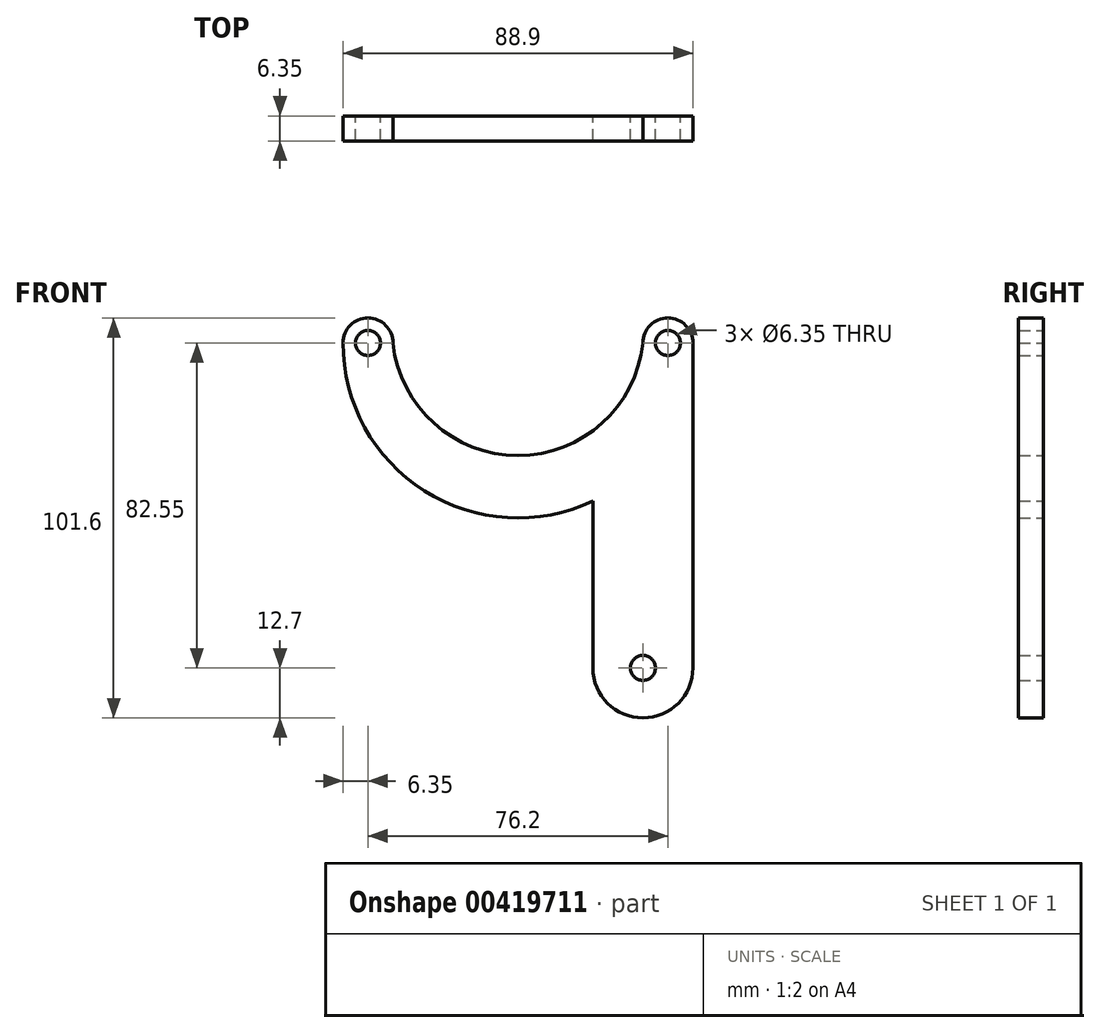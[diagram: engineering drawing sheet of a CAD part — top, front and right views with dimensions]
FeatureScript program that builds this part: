
annotation { "Feature Type Name" : "Feature", "Feature Type Description" : "" }
export const myFeature = defineFeature(function(context is Context, id is Id, definition is map)
    precondition{}
    {
        {
            var Q0;
            Q0=qCreatedBy(makeId("Front.planeOp"),FACE);
            var sketch = newSketch(context, id + "F0", { "sketchPlane" : qUnion([Q0])});
            skLineSegment(sketch, "E0", {"start": v(0, 0) * mm, "end": v(38.1, 0) * mm});
            skLineSegment(sketch, "E1", {"start": v(38.1, 0) * mm, "end": v(0, 0) * mm});
            skLineSegment(sketch, "E2", {"start": v(-38.1, 0) * mm, "end": v(0, 0) * mm});
            skCircle(sketch, "E3", {"center": v(-38.1, 0) * mm, "radius": 6.35 * mm});
            skCircle(sketch, "E4", {"center": v(38.1, 0) * mm, "radius": 6.35 * mm});
            skCircle(sketch, "E5", {"center": v(0, 0) * mm, "radius": 44.45 * mm});
            skLineSegment(sketch, "E6", {"start": v(0, 0) * mm, "end": v(0, -28.58) * mm});
            skLineSegment(sketch, "E7", {"start": v(-38.1, 0) * mm, "end": v(-31.75, 0) * mm});
            skLineSegment(sketch, "E8", {"start": v(38.1, 0) * mm, "end": v(31.75, 0) * mm});
            skArc(sketch, "E9", {"start": v(-31.75, 0) * mm, "mid": v(0, -28.58) * mm, "end": v(31.75, 0) * mm});
            skLineSegment(sketch, "E10", {"start": v(31.75, 0) * mm, "end": v(31.75, -82.55) * mm});
            skPoint(sketch, "E11", {"position": v(31.75, -82.55) * mm});
            skLineSegment(sketch, "E12", {"start": v(0, -44.45) * mm, "end": v(44.45, -44.45) * mm});
            skLineSegment(sketch, "E13", {"start": v(0, -44.45) * mm, "end": v(-52.8, -44.45) * mm});
            skCircle(sketch, "E14", {"center": v(31.75, -82.55) * mm, "radius": 12.7 * mm});
            skLineSegment(sketch, "E15", {"start": v(31.75, -82.55) * mm, "end": v(19.05, -82.55) * mm});
            skLineSegment(sketch, "E16", {"start": v(31.75, -82.55) * mm, "end": v(44.45, -82.55) * mm});
            skLineSegment(sketch, "E17", {"start": v(44.45, -82.55) * mm, "end": v(44.45, 0) * mm});
            skLineSegment(sketch, "E18", {"start": v(19.05, -82.55) * mm, "end": v(19.05, -40.16) * mm});
            skSolve(sketch);
        }
        {
            var Q0;
            {var subQ0=sQuery(id+"F0.wireOp",EDGE,"E3");var subQ2=makeQuery(id+"F0.imprint","INTERSECT",VERTEX,{"derivedFrom":[subQ0,sQuery(id+"F0.wireOp",EDGE,"E5")]});Q0=makeQuery(id+"F0.imprint","IMPRINT",FACE,{"disambiguationData":[TD([[makeQuery(id+"F0.imprint","IMPRINT",EDGE,{"disambiguationData":[TD([[subQ2,1.0]])],"derivedFrom":subQ0}),1.0]])]});}
            var Q1;
            {var subQ4=sQuery(id+"F0.wireOp",EDGE,"E5");var subQ5=makeQuery(id+"F0.imprint","INTERSECT",VERTEX,{"derivedFrom":[subQ4,sQuery(id+"F0.wireOp",EDGE,"XhDido47-JSk9-PN7a-mwUm-eUsiFU9qKRD5")]});Q1=makeQuery(id+"F0.imprint","IMPRINT",FACE,{"disambiguationData":[TD([[makeQuery(id+"F0.imprint","IMPRINT",EDGE,{"disambiguationData":[TD([[subQ5,1.0]])],"derivedFrom":subQ4}),1.0]])]});}
            var Q2;
            {var subQ0=sQuery(id+"F0.wireOp",EDGE,"E4");var subQ2=makeQuery(id+"F0.imprint","INTERSECT",VERTEX,{"derivedFrom":[subQ0,sQuery(id+"F0.wireOp",EDGE,"E5"),sQuery(id+"F0.wireOp",EDGE,"RHOj4S1e-cnUz-p6yP-vj5Y-QZDLPZyhU6kP")]});Q2=makeQuery(id+"F0.imprint","IMPRINT",FACE,{"disambiguationData":[TD([[makeQuery(id+"F0.imprint","IMPRINT",EDGE,{"disambiguationData":[TD([[subQ2,-1.0]])],"derivedFrom":subQ0}),1.0]])]});}
            var Q3;
            {var subQ0=sQuery(id+"F0.wireOp",EDGE,"E10");var subQ3=sQuery(id+"F0.wireOp",EDGE,"E5");var subQ5=makeQuery(id+"F0.imprint","INTERSECT",VERTEX,{"derivedFrom":[subQ3,subQ0]});Q3=makeQuery(id+"F0.imprint","IMPRINT",FACE,{"disambiguationData":[TD([[makeQuery(id+"F0.imprint","IMPRINT",EDGE,{"disambiguationData":[TD([[subQ5,-1.0]])],"derivedFrom":subQ3}),1.0]])]});}
            var Q4;
            {var subQ0=sQuery(id+"F0.wireOp",EDGE,"RHOj4S1e-cnUz-p6yP-vj5Y-QZDLPZyhU6kP");Q4=makeQuery(id+"F0.imprint","IMPRINT",FACE,{"disambiguationData":[TD([[makeQuery(id+"F0.imprint","IMPRINT",EDGE,{"derivedFrom":subQ0}),-1.0]])]});}
            var Q5;
            {var subQ0=sQuery(id+"F0.wireOp",EDGE,"XhDido47-JSk9-PN7a-mwUm-eUsiFU9qKRD5");Q5=makeQuery(id+"F0.imprint","IMPRINT",FACE,{"disambiguationData":[TD([[makeQuery(id+"F0.imprint","IMPRINT",EDGE,{"derivedFrom":subQ0}),-1.0]])]});}
            var Q6;
            {var subQ0=sQuery(id+"F0.wireOp",EDGE,"3i2DmJEj-DKhP-iJt3-PwoP-cG0X3qstrTAl");Q6=makeQuery(id+"F0.imprint","IMPRINT",FACE,{"disambiguationData":[TD([[makeQuery(id+"F0.imprint","IMPRINT",EDGE,{"derivedFrom":subQ0}),-1.0]])]});}
            var Q7;
            {var subQ0=sQuery(id+"F0.wireOp",EDGE,"CGOJktKc-CADg-FGEi-2G2Y-Sdd0SxkiLkLI");Q7=makeQuery(id+"F0.imprint","IMPRINT",FACE,{"disambiguationData":[TD([[makeQuery(id+"F0.imprint","IMPRINT",EDGE,{"derivedFrom":subQ0}),1.0]])]});}
            var Q8;
            {var subQ0=sQuery(id+"F0.wireOp",EDGE,"3i2DmJEj-DKhP-iJt3-PwoP-cG0X3qstrTAl");Q8=makeQuery(id+"F0.imprint","IMPRINT",FACE,{"disambiguationData":[TD([[makeQuery(id+"F0.imprint","IMPRINT",EDGE,{"derivedFrom":subQ0}),1.0]])]});}
            var Q9;
            {var subQ0=sQuery(id+"F0.wireOp",EDGE,"E18");var subQ1=sQuery(id+"F0.wireOp",EDGE,"E5");var subQ2=makeQuery(id+"F0.imprint","INTERSECT",VERTEX,{"derivedFrom":[subQ1,subQ0]});Q9=makeQuery(id+"F0.imprint","IMPRINT",FACE,{"disambiguationData":[TD([[makeQuery(id+"F0.imprint","IMPRINT",EDGE,{"disambiguationData":[TD([[subQ2,-1.0]])],"derivedFrom":subQ1}),-1.0]])]});}
            var Q10;
            {var subQ1=sQuery(id+"F0.wireOp",EDGE,"E5");var subQ3=sQuery(id+"F0.wireOp",EDGE,"E10");var subQ4=makeQuery(id+"F0.imprint","INTERSECT",VERTEX,{"derivedFrom":[subQ1,subQ3]});Q10=makeQuery(id+"F0.imprint","IMPRINT",FACE,{"disambiguationData":[TD([[makeQuery(id+"F0.imprint","IMPRINT",EDGE,{"disambiguationData":[TD([[subQ4,-1.0]])],"derivedFrom":subQ3}),1.0]])]});}
            var Q11;
            {var subQ0=sQuery(id+"F0.wireOp",EDGE,"E12");var subQ1=sQuery(id+"F0.wireOp",EDGE,"E10");var subQ2=makeQuery(id+"F0.imprint","INTERSECT",VERTEX,{"derivedFrom":[subQ1,subQ0]});Q11=makeQuery(id+"F0.imprint","IMPRINT",FACE,{"disambiguationData":[TD([[makeQuery(id+"F0.imprint","IMPRINT",EDGE,{"disambiguationData":[TD([[subQ2,-1.0]])],"derivedFrom":subQ1}),1.0]])]});}
            var Q12;
            {var subQ0=sQuery(id+"F0.wireOp",EDGE,"E12");var subQ1=sQuery(id+"F0.wireOp",EDGE,"E10");var subQ2=makeQuery(id+"F0.imprint","INTERSECT",VERTEX,{"derivedFrom":[subQ1,subQ0]});Q12=makeQuery(id+"F0.imprint","IMPRINT",FACE,{"disambiguationData":[TD([[makeQuery(id+"F0.imprint","IMPRINT",EDGE,{"disambiguationData":[TD([[subQ2,-1.0]])],"derivedFrom":subQ1}),-1.0]])]});}
            var Q13;
            {var subQ0=sQuery(id+"F0.wireOp",EDGE,"E15");Q13=makeQuery(id+"F0.imprint","IMPRINT",FACE,{"disambiguationData":[TD([[makeQuery(id+"F0.imprint","IMPRINT",EDGE,{"derivedFrom":subQ0}),-1.0]])]});}
            var Q14;
            {var subQ0=sQuery(id+"F0.wireOp",EDGE,"E16");Q14=makeQuery(id+"F0.imprint","IMPRINT",FACE,{"disambiguationData":[TD([[makeQuery(id+"F0.imprint","IMPRINT",EDGE,{"derivedFrom":subQ0}),1.0]])]});}
            var Q15;
            {var subQ0=sQuery(id+"F0.wireOp",EDGE,"E15");Q15=makeQuery(id+"F0.imprint","IMPRINT",FACE,{"disambiguationData":[TD([[makeQuery(id+"F0.imprint","IMPRINT",EDGE,{"derivedFrom":subQ0}),1.0]])]});}
            extrude(context, id + "F1", {"entities" : qUnion([Q0, Q1, Q2, Q3, Q4, Q5, Q6, Q7, Q8, Q9, Q10, Q11, Q12, Q13, Q14, Q15]), "depth" : 6.35 * mm, "offsetDistance" : 25.4 * mm});
        }
        {
            var Q0;
            Q0=sQuery(id+"F0.wireOp",VERTEX,"E3.center");
            var Q1;
            Q1=sQuery(id+"F0.wireOp",VERTEX,"E4.center");
            var Q2;
            Q2=sQuery(id+"F0.wireOp",VERTEX,"E11");
            var Q3;
            Q3=makeQuery(id+"F1.opExtrude","SWEPT_BODY",BODY,{"disambiguationData":[OSD([sQuery(id+"F0.wireOp",EDGE,"E3"),sQuery(id+"F0.wireOp",EDGE,"E4"),sQuery(id+"F0.wireOp",EDGE,"E5"),sQuery(id+"F0.wireOp",EDGE,"E9"),sQuery(id+"F0.wireOp",EDGE,"RHOj4S1e-cnUz-p6yP-vj5Y-QZDLPZyhU6kP"),sQuery(id+"F0.wireOp",EDGE,"XhDido47-JSk9-PN7a-mwUm-eUsiFU9qKRD5"),sQuery(id+"F0.wireOp",EDGE,"VNrWbGNr-6td4-PTVr-zRXs-djld0Izz6bXE")])]});
            hole(context, id + "F2", {"style" : HoleStyle.SIMPLE, "endStyle" : HoleEndStyle.THROUGH, "oppositeDirection" : true, "holeDiameter" : 6.35 * mm, "majorDiameter" : 6.35 * mm, "isTappedThrough" : true, "tappedDepth" : 12.7 * mm, "tapClearance" : 3, "locations" : qUnion([Q0, Q1, Q2]), "scope" : qUnion([Q3])});
        }
    });
